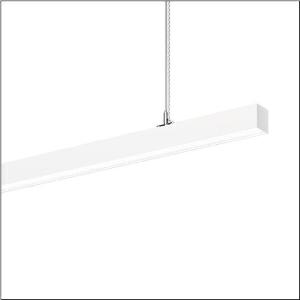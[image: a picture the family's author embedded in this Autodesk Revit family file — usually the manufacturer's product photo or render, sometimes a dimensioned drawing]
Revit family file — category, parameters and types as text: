
# Revit family: silica_r__21_51mx33tat7w_2751
name_source: partatom
category: Lighting Fixtures
units: mm (PartAtom-declared; Revit-internal decimal feet)

## family parameters
Cut with Voids When Loaded = No
Host = Face
Light Source = No
Part Type = Normal
Room Calculation Point = No
Round Connector Dimension = Use Diameter
Shared = No

## types (1)
- --- (1 x LED, 5740 lm, 53.8 W, 6500K)
    Apparent Load = 54 VA
    CIE Flux Codes = 78 96 99 56 100
    Color Rendering = 80
    Color Temperature = 6500K
    Default Elevation = 1800 mm
    Description = Silica® 21, office luminaire, primary optical cover: prismatic diffuser, of PMMA, CAT 2 (L<= 3000cd/m²), light emission: direct/indirect distribution, primary light characteristic: symmetric, installation type: suspended mounting, LED, rated luminous flux: 5.740lm, luminous efficacy: 102lm/W, light colour: 8tw, colour temperature: 2700..6500K, control gear: ECG DALI, with terminal, 3+2-pole, max. 2.5mm², mains connection: 220..240V, AC, 50/60Hz, rated input power: 56.5W, luminaire housing, of aluminium, traffic white (RAL 9016), length: 1.204mm, width: 53mm, height: 53mm, protection rating (complete): IP20, insulation class (complete): insulation class I (protective earthing), certification: CE, permissible operating ambient temperature: 0..+35°C, standard: EN 50419, packaging unit: 1 piece
    Height = 53 mm
    Lamp = 1 x LED
    Lamp Light Flux = 5740 lm
    Lamp Power = 53.8 W
    Lamp count = 1
    Length = 1204 mm
    Luminous efficacy = 107 lm/W
    Manufacturer = Siteco
    ModVariant = No
    Model = 51MX33TAT7W
    Mounting Place = Ceiling
    Mounting Type = Pendant
    Number of Poles = 1
    OnlyDefault = Yes
    Power Factor = 1
    Product Name = Silica® 21
    Product group = office luminaire | ceiling pendant
    ProductGroupID = 902
    Protection Class = Protection class I
    Protection Degree = IP 20
    RLX_Detail_Level = 1
    RLX_Emergency_Light_Flux = 0 lm
    RLX_Emergency_Type = 0
    RLX_Emergency_Type_DB = No
    RlxData = <blob elided: 18221 chars, md5=462f879f>
    Socket = socket
    Standby Power = 0 W
    System Light Flux = 5740 lm
    System Power = 54 W
    Type Comments = individual setting
    Type Image = l_1335916.jpg
    URL = http://relux.com
    VarID = @adj_109585
    Voltage = 0 V
    Weight = 0.00 kg
    Width = 53 mm

## geometry (parser evidence)
native form markers: Blend x4, Sweep x12
no freeform markers — native parametric forms only
